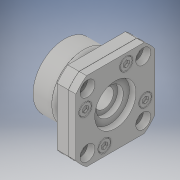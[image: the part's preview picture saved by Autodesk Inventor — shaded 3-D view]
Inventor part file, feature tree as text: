
AUTODESK INVENTOR PART (.ipt)
format: ipt  version: 2021 (Build 250183000, 183)  size: 326,144 bytes
history: native  units: mm
features: other x28, sketch x7, revolve x4, extrude x4, pattern_linear x3, hole x1
ambient origin geometry x8: Origin, YZ Plane, XZ Plane, XY Plane, X Axis, Y Axis, Z Axis, Center Point
bodies: Solid1 (feature_tree)
feature tree (47):
  revolve  "Revolution1"  [1 undecoded]
  extrude  "Extrusion1"  TaperAngle=360.0deg  [1 undecoded]
  revolve  "Revolution2"  [1 undecoded]
  revolve  "Revolution3"  [1 undecoded]
  revolve  "Revolution4"  [1 undecoded]
  hole  "Hole1"  [1 undecoded]
  pattern_linear  "Rectangular Pattern1"  [2 undecoded]
  extrude  "Extrusion2"  [1 undecoded]
  extrude  "Extrusion3"  [1 undecoded]
  pattern_linear  "Rectangular Pattern2"  [2 undecoded]
  extrude  "Extrusion4"  [1 undecoded]
  pattern_linear  "Rectangular Pattern3"  [2 undecoded]
  other  "_to_bjs_XY"
  other  "_to_bjs_YZ"
  other  "_to_bjs_ZX"
  other  "_to_bjs_X"
  other  "_to_bjs_Y"
  other  "_to_bjs_Z"
  other  "_to_bjs_Center"
  other  "to_collar_XY"
  other  "to_collar_YZ"
  other  "to_collar_ZX"
  other  "to_collar_X"
  other  "to_collar_Y"
  other  "to_collar_Z"
  other  "to_collar_Center"
  other  "to_collar_2_XY"
  other  "to_collar_2_YZ"
  other  "to_collar_2_ZX"
  other  "to_collar_2_X"
  other  "to_collar_2_Y"
  other  "to_collar_2_Z"
  other  "to_collar_2_Center"
  other  "to_dummy_XY"
  other  "to_dummy_YZ"
  other  "to_dummy_ZX"
  other  "to_dummy_X"
  other  "to_dummy_Y"
  other  "to_dummy_Z"
  other  "to_dummy_Center"
  sketch  "Sketch_1"  dims[d0=360.0deg d1=10.0mm d2=0.0mm]
  sketch  "Sketch_2"  dims[d3=360.0deg d4=360.0deg]
  sketch  "Sketch_5"  dims[d5=360.0deg]
  sketch  "Sketch6"  dims[d6=4.5mm d7=6.0mm d8=8.0mm d9=4.0mm d10=90.0deg d11=10.0mm d12=0.0mm d13=20.0mm d15=29.698485mm d16=20.0mm d18=29.698485mm]
  sketch  "Sketch_9"  dims[d19=0.05mm d20=0.0mm d21=1.0mm d22=0.0mm]
  sketch  "Sketch_10"  dims[d23=20.0mm d25=24.041631mm d26=20.0mm d28=24.041631mm d29=1.0mm d30=0.0mm]
  sketch  "Sketch_12"  dims[d31=20.0mm d33=24.041631mm d34=20.0mm d36=24.041631mm d37=0.0mm d38=0.0mm d39=0.0mm d40=0.0mm]
note: 15 required parameter values undecoded (feature->parameter linkage not recoverable at this tier; creation-order binding heuristic only, values carry confidence <= 0.55)